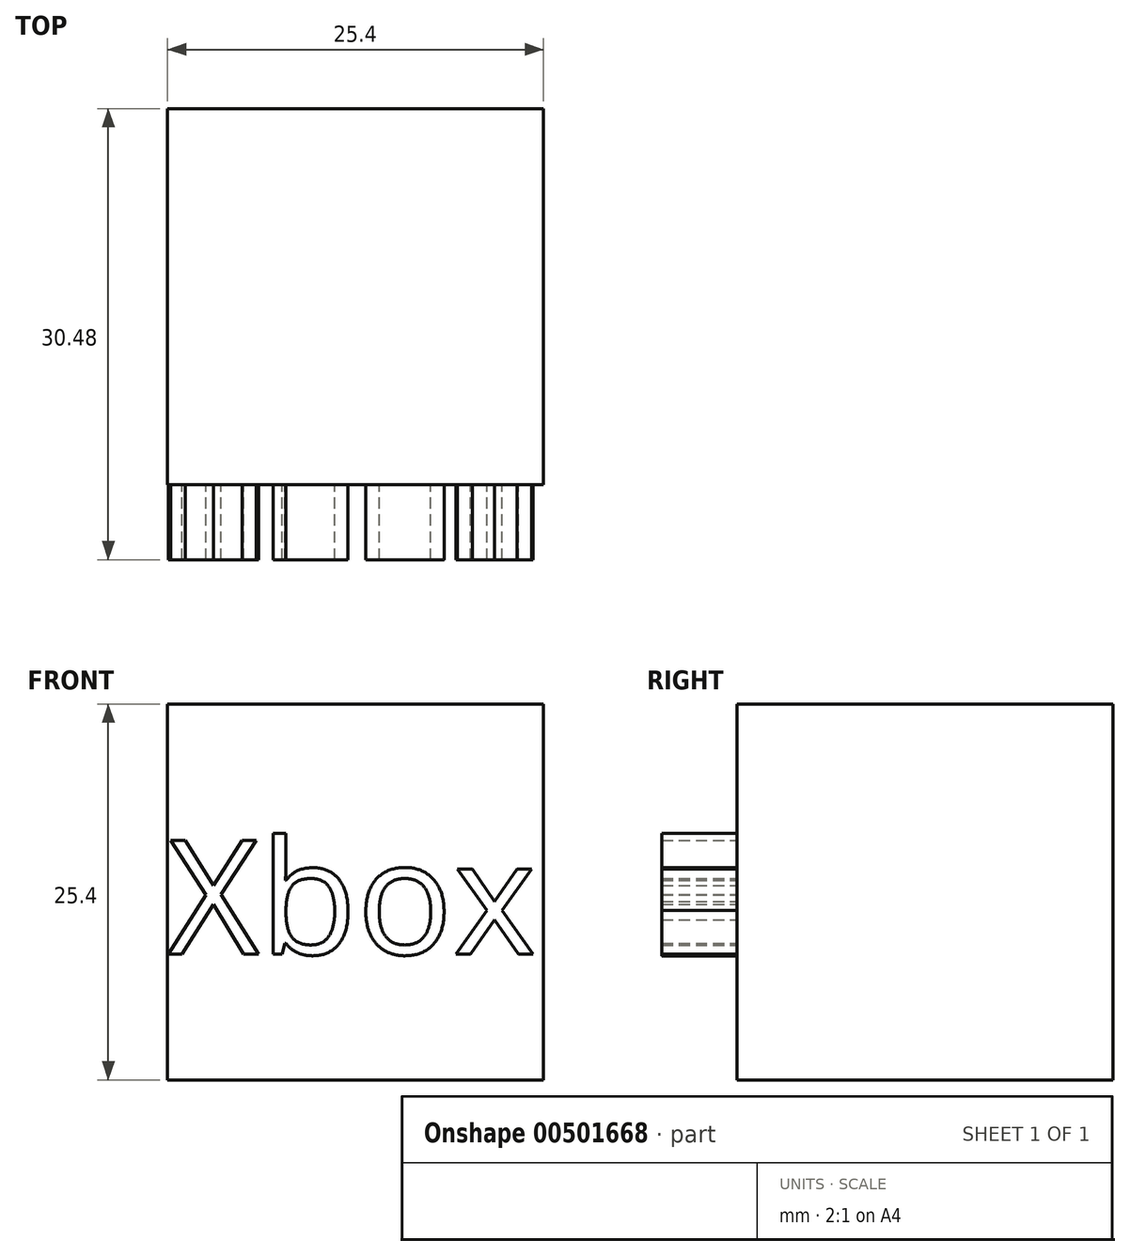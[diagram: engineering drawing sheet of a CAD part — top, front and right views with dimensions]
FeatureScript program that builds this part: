
annotation { "Feature Type Name" : "Feature", "Feature Type Description" : "" }
export const myFeature = defineFeature(function(context is Context, id is Id, definition is map)
    precondition{}
    {
        {
            var Q0;
            Q0=qCreatedBy(makeId("Front.planeOp"),FACE);
            var sketch = newSketch(context, id + "F0", { "sketchPlane" : qUnion([Q0])});
            skLineSegment(sketch, "E0.bottom", {"start": v(0, 0) * mm, "end": v(25.4, 0) * mm});
            skLineSegment(sketch, "E0.top", {"start": v(0, 25.4) * mm, "end": v(25.4, 25.4) * mm});
            skLineSegment(sketch, "E0.left", {"start": v(0, 0) * mm, "end": v(0, 25.4) * mm});
            skLineSegment(sketch, "E0.right", {"start": v(25.4, 0) * mm, "end": v(25.4, 25.4) * mm});
            skSolve(sketch);
        }
        {
            var Q0;
            Q0=makeQuery(id+"F0.imprint","IMPRINT",FACE,{"disambiguationData":[TD([[makeQuery(id+"F0.imprint","IMPRINT",EDGE,{"derivedFrom":sQuery(id+"F0.wireOp",EDGE,"E0.bottom")}),1.0]])]});
            extrude(context, id + "F1", {"entities" : qUnion([Q0]), "depth" : 25.4 * mm});
        }
        {
            var Q0;
            Q0=makeQuery(id+"F1.opExtrude","CAP_FACE",FACE,{"disambiguationData":[OSD([sQuery(id+"F0.wireOp",EDGE,"E0.bottom"),sQuery(id+"F0.wireOp",EDGE,"E0.top"),sQuery(id+"F0.wireOp",EDGE,"E0.left"),sQuery(id+"F0.wireOp",EDGE,"E0.right")])],"isStart":false});
            var sketch = newSketch(context, id + "F2", { "sketchPlane" : qUnion([Q0])});
            skText(sketch, "E1", { "text": "Xbox", "fontName": "OpenSans-Regular.ttf"});
            const initialGuessF2  = {"E1": [0, 0.00849, 1, 0, 0.00774]};
            skSetInitialGuess(sketch, initialGuessF2);
            skSolve(sketch);
        }
        {
            var Q0;
            Q0 = qSketchRegion(id + "F2", true);
            extrude(context, id + "F3", {"entities" : qUnion([Q0]), "operationType" : NewBodyOperationType.ADD, "depth" : 5.08 * mm});
        }
    });
